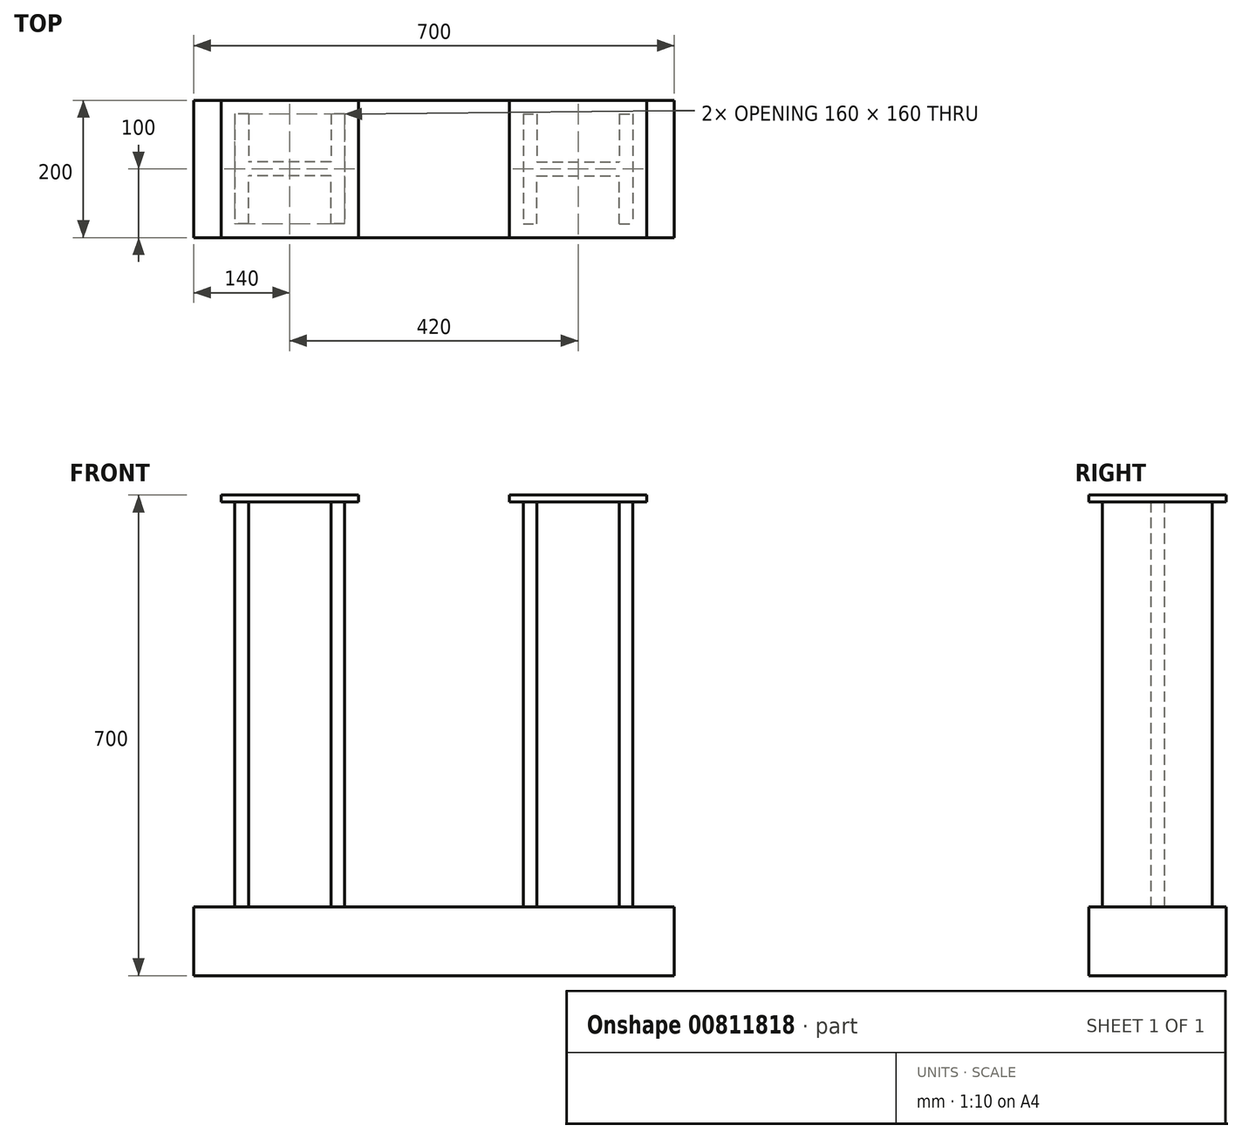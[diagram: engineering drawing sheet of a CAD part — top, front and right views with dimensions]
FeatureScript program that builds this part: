
annotation { "Feature Type Name" : "Feature", "Feature Type Description" : "" }
export const myFeature = defineFeature(function(context is Context, id is Id, definition is map)
    precondition{}
    {
        {
            var Q0;
            Q0=qCreatedBy(makeId("Front.planeOp"),FACE);
            var sketch = newSketch(context, id + "F0", { "sketchPlane" : qUnion([Q0])});
            skLineSegment(sketch, "E0.bottom", {"start": v(0, 0) * mm, "end": v(350, 0) * mm});
            skLineSegment(sketch, "E0.top", {"start": v(0, 100) * mm, "end": v(350, 100) * mm});
            skLineSegment(sketch, "E0.left", {"start": v(0, 0) * mm, "end": v(0, 100) * mm});
            skLineSegment(sketch, "E0.right", {"start": v(350, 0) * mm, "end": v(350, 100) * mm});
            skLineSegment(sketch, "E1.MirrorCS", {"start": v(0, 0) * mm, "end": v(-350, 0) * mm});
            skLineSegment(sketch, "E2.MirrorCS", {"start": v(0, 100) * mm, "end": v(-350, 100) * mm});
            skLineSegment(sketch, "E3.MirrorCS", {"start": v(-350, 0) * mm, "end": v(-350, 100) * mm});
            skSolve(sketch);
        }
        {
            var Q0;
            Q0=makeQuery(id+"F0.imprint","IMPRINT",FACE,{"disambiguationData":[TD([[makeQuery(id+"F0.imprint","IMPRINT",EDGE,{"derivedFrom":sQuery(id+"F0.wireOp",EDGE,"E0.left")}),1.0]])]});
            var Q1;
            Q1=makeQuery(id+"F0.imprint","IMPRINT",FACE,{"disambiguationData":[TD([[makeQuery(id+"F0.imprint","IMPRINT",EDGE,{"derivedFrom":sQuery(id+"F0.wireOp",EDGE,"E0.bottom")}),1.0]])]});
            extrude(context, id + "F1", {"entities" : qUnion([Q0, Q1]), "depth" : 200 * mm, "offsetDistance" : 25 * mm});
        }
        {
            var Q0;
            Q0=makeQuery(id+"F1.opExtrude","SWEPT_FACE",FACE,{"disambiguationData":[OSD([sQuery(id+"F0.wireOp",EDGE,"E0.top"),sQuery(id+"F0.wireOp",EDGE,"E2.MirrorCS")])]});
            var sketch = newSketch(context, id + "F2", { "sketchPlane" : qUnion([Q0])});
            skLineSegment(sketch, "E4.bottom", {"start": v(130, -20) * mm, "end": v(290, -20) * mm});
            skLineSegment(sketch, "E4.top", {"start": v(130, -180) * mm, "end": v(290, -180) * mm});
            skLineSegment(sketch, "E4.left", {"start": v(130, -20) * mm, "end": v(130, -180) * mm});
            skLineSegment(sketch, "E4.right", {"start": v(290, -20) * mm, "end": v(290, -180) * mm});
            skLineSegment(sketch, "E5.bottom", {"start": v(150, -20) * mm, "end": v(270, -20) * mm});
            skLineSegment(sketch, "E5.top", {"start": v(150, -90) * mm, "end": v(270, -90) * mm});
            skLineSegment(sketch, "E5.left", {"start": v(150, -20) * mm, "end": v(150, -90) * mm});
            skLineSegment(sketch, "E5.right", {"start": v(270, -20) * mm, "end": v(270, -90) * mm});
            skLineSegment(sketch, "E6.bottom", {"start": v(150, -180) * mm, "end": v(270, -180) * mm});
            skLineSegment(sketch, "E6.top", {"start": v(150, -110) * mm, "end": v(270, -110) * mm});
            skLineSegment(sketch, "E6.left", {"start": v(150, -180) * mm, "end": v(150, -110) * mm});
            skLineSegment(sketch, "E6.right", {"start": v(270, -180) * mm, "end": v(270, -110) * mm});
            skLineSegment(sketch, "E7.MirrorCS", {"start": v(-130, -20) * mm, "end": v(-130, -180) * mm});
            skLineSegment(sketch, "E8.MirrorCS", {"start": v(-150, -20) * mm, "end": v(-150, -90) * mm});
            skLineSegment(sketch, "E9.MirrorCS", {"start": v(-130, -20) * mm, "end": v(-290, -20) * mm});
            skLineSegment(sketch, "E10.MirrorCS", {"start": v(-150, -180) * mm, "end": v(-270, -180) * mm});
            skLineSegment(sketch, "E11.MirrorCS", {"start": v(-270, -20) * mm, "end": v(-270, -90) * mm});
            skLineSegment(sketch, "E12.MirrorCS", {"start": v(-150, -90) * mm, "end": v(-270, -90) * mm});
            skLineSegment(sketch, "E13.MirrorCS", {"start": v(-150, -20) * mm, "end": v(-270, -20) * mm});
            skLineSegment(sketch, "E14.MirrorCS", {"start": v(-130, -180) * mm, "end": v(-290, -180) * mm});
            skLineSegment(sketch, "E15.MirrorCS", {"start": v(-150, -110) * mm, "end": v(-270, -110) * mm});
            skLineSegment(sketch, "E16.MirrorCS", {"start": v(-150, -180) * mm, "end": v(-150, -110) * mm});
            skLineSegment(sketch, "E17.MirrorCS", {"start": v(-270, -180) * mm, "end": v(-270, -110) * mm});
            skLineSegment(sketch, "E18.MirrorCS", {"start": v(-290, -20) * mm, "end": v(-290, -180) * mm});
            skSolve(sketch);
        }
        {
            var Q0;
            {var subQ1=sQuery(id+"F2.wireOp",EDGE,"E11.MirrorCS");Q0=makeQuery(id+"F2.imprint","IMPRINT",FACE,{"disambiguationData":[TD([[makeQuery(id+"F2.imprint","IMPRINT",EDGE,{"derivedFrom":subQ1}),-1.0]])]});}
            var Q1;
            {var subQ3=sQuery(id+"F2.wireOp",EDGE,"E4.left");Q1=makeQuery(id+"F2.imprint","IMPRINT",FACE,{"disambiguationData":[TD([[makeQuery(id+"F2.imprint","IMPRINT",EDGE,{"derivedFrom":subQ3}),1.0]])]});}
            extrude(context, id + "F3", {"entities" : qUnion([Q0, Q1]), "operationType" : NewBodyOperationType.ADD, "depth" : 600 * mm, "offsetDistance" : 25 * mm});
        }
        {
            var Q0;
            Q0=makeQuery(id+"F3.opExtrude","CAP_FACE",FACE,{"disambiguationData":[OSD([sQuery(id+"F2.wireOp",EDGE,"E4.bottom"),sQuery(id+"F2.wireOp",EDGE,"E4.top"),sQuery(id+"F2.wireOp",EDGE,"E4.left"),sQuery(id+"F2.wireOp",EDGE,"E4.right"),sQuery(id+"F2.wireOp",EDGE,"E5.top"),sQuery(id+"F2.wireOp",EDGE,"E5.left"),sQuery(id+"F2.wireOp",EDGE,"E5.right"),sQuery(id+"F2.wireOp",EDGE,"E6.top"),sQuery(id+"F2.wireOp",EDGE,"E6.left"),sQuery(id+"F2.wireOp",EDGE,"E6.right")])],"isStart":false});
            var sketch = newSketch(context, id + "F4", { "sketchPlane" : qUnion([Q0])});
            skLineSegment(sketch, "E19.bottom", {"start": v(-310, 0) * mm, "end": v(-110, 0) * mm});
            skLineSegment(sketch, "E19.top", {"start": v(-310, -200) * mm, "end": v(-110, -200) * mm});
            skLineSegment(sketch, "E19.left", {"start": v(-310, 0) * mm, "end": v(-310, -200) * mm});
            skLineSegment(sketch, "E19.right", {"start": v(-110, 0) * mm, "end": v(-110, -200) * mm});
            skLineSegment(sketch, "E20.MirrorCS", {"start": v(110, 0) * mm, "end": v(110, -200) * mm});
            skLineSegment(sketch, "E21.MirrorCS", {"start": v(310, 0) * mm, "end": v(310, -200) * mm});
            skLineSegment(sketch, "E22.MirrorCS", {"start": v(310, 0) * mm, "end": v(110, 0) * mm});
            skLineSegment(sketch, "E23.MirrorCS", {"start": v(310, -200) * mm, "end": v(110, -200) * mm});
            skSolve(sketch);
        }
        {
            var Q0;
            Q0=makeQuery(id+"F4.imprint","IMPRINT",FACE,{"disambiguationData":[TD([[makeQuery(id+"F4.imprint","IMPRINT",EDGE,{"derivedFrom":sQuery(id+"F4.wireOp",EDGE,"E20.MirrorCS")}),1.0]])]});
            var Q1;
            {var subQ3=sQuery(id+"F2.wireOp",EDGE,"E4.left");Q1=makeQuery(id+"F4.imprint","IMPRINT",FACE,{"disambiguationData":[TD([[makeQuery(id+"F4.imprint","IMPRINT",EDGE,{"derivedFrom":makeQuery(id+"F3.opExtrude","CAP_EDGE",EDGE,{"disambiguationData":[OSD([subQ3])],"isStart":false})}),1.0]])]});}
            var Q2;
            Q2=makeQuery(id+"F4.imprint","IMPRINT",FACE,{"disambiguationData":[TD([[makeQuery(id+"F4.imprint","IMPRINT",EDGE,{"derivedFrom":sQuery(id+"F4.wireOp",EDGE,"E19.bottom")}),-1.0]])]});
            extrude(context, id + "F5", {"entities" : qUnion([Q0, Q1, Q2]), "operationType" : NewBodyOperationType.ADD, "oppositeDirection" : true, "depth" : 10 * mm, "offsetDistance" : 25 * mm});
        }
    });
